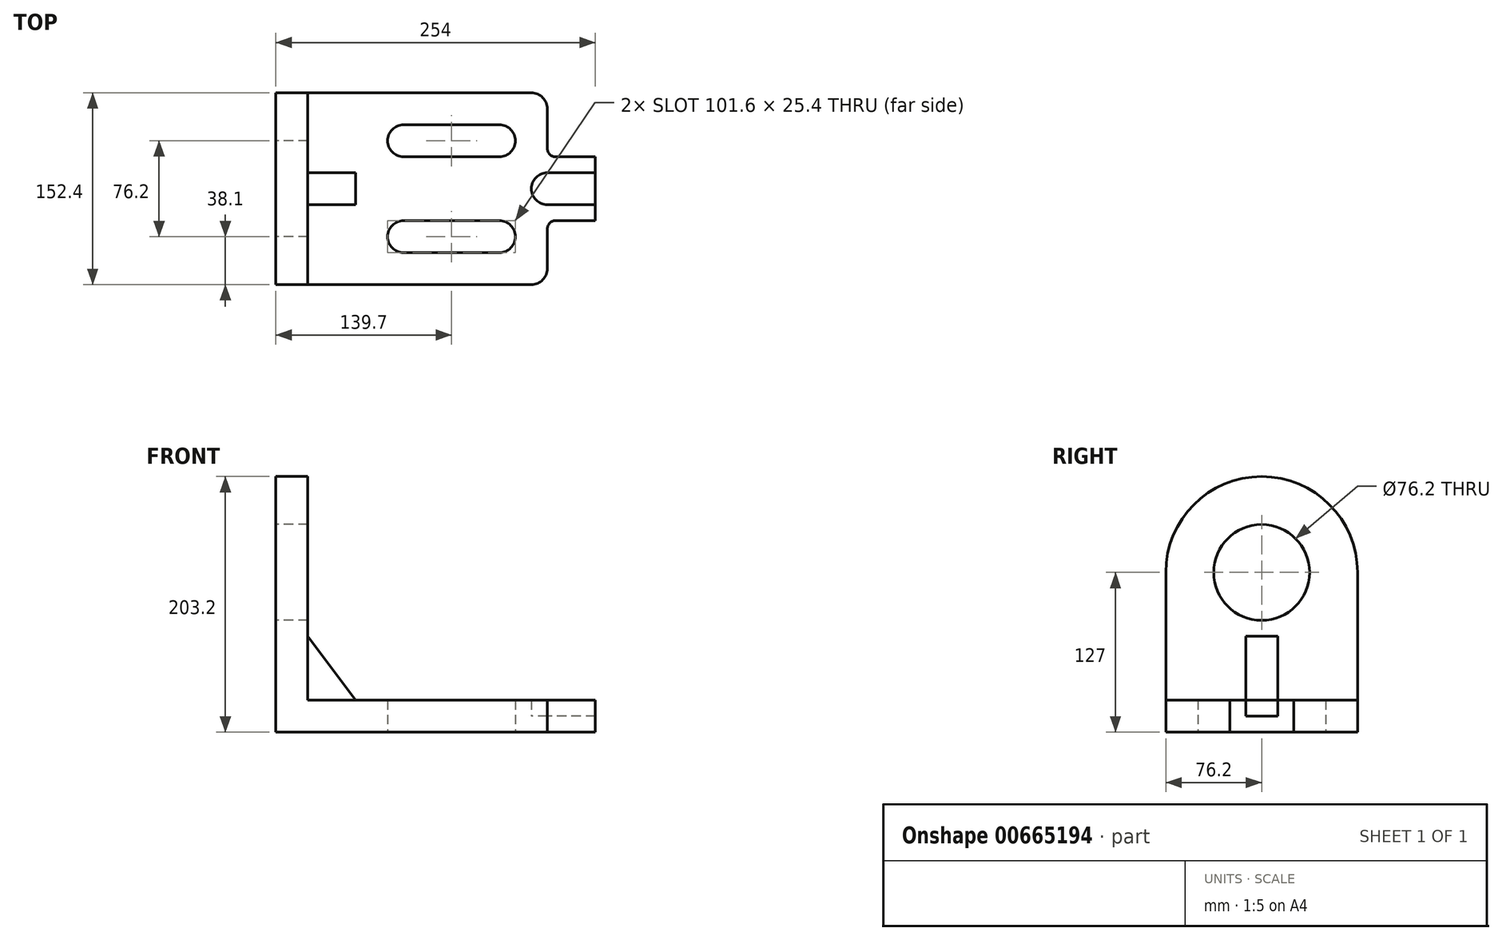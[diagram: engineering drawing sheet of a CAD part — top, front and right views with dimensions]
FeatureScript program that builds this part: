
annotation { "Feature Type Name" : "Feature", "Feature Type Description" : "" }
export const myFeature = defineFeature(function(context is Context, id is Id, definition is map)
    precondition{}
    {
        {
            var Q0;
            Q0=qCreatedBy(makeId("Top.planeOp"),FACE);
            var sketch = newSketch(context, id + "F0", { "sketchPlane" : qUnion([Q0])});
            skLineSegment(sketch, "E0", {"start": v(0, 0) * mm, "end": v(203.2, 0) * mm});
            skLineSegment(sketch, "E1", {"start": v(215.9, 12.7) * mm, "end": v(215.9, 44.45) * mm});
            skLineSegment(sketch, "E2", {"start": v(222.25, 50.8) * mm, "end": v(254, 50.8) * mm});
            skLineSegment(sketch, "E3", {"start": v(254, 50.8) * mm, "end": v(254, 63.5) * mm});
            skLineSegment(sketch, "E4", {"start": v(254, 63.5) * mm, "end": v(215.9, 63.5) * mm});
            skLineSegment(sketch, "E5", {"start": v(215.9, 88.9) * mm, "end": v(254, 88.9) * mm});
            skLineSegment(sketch, "E6", {"start": v(254, 88.9) * mm, "end": v(254, 101.6) * mm});
            skLineSegment(sketch, "E7", {"start": v(254, 101.6) * mm, "end": v(222.25, 101.6) * mm});
            skLineSegment(sketch, "E8", {"start": v(215.9, 107.95) * mm, "end": v(215.9, 139.7) * mm});
            skLineSegment(sketch, "E9", {"start": v(203.2, 152.4) * mm, "end": v(0, 152.4) * mm});
            skLineSegment(sketch, "E10", {"start": v(0, 152.4) * mm, "end": v(0, 0) * mm});
            skPoint(sketch, "E11.visualSharp", {"position": v(215.9, 152.4) * mm});
            skArc(sketch, "E11.filletArc", {"start": v(215.9, 139.7) * mm, "mid": v(212.18, 148.68) * mm, "end": v(203.2, 152.4) * mm});
            skPoint(sketch, "E12.visualSharp", {"position": v(215.9, 0) * mm});
            skArc(sketch, "E12.filletArc", {"start": v(203.2, 0) * mm, "mid": v(212.18, 3.72) * mm, "end": v(215.9, 12.7) * mm});
            skPoint(sketch, "E13.visualSharp", {"position": v(215.9, 50.8) * mm});
            skArc(sketch, "E13.filletArc", {"start": v(222.25, 50.8) * mm, "mid": v(217.76, 48.94) * mm, "end": v(215.9, 44.45) * mm});
            skPoint(sketch, "E14.visualSharp", {"position": v(215.9, 101.6) * mm});
            skArc(sketch, "E14.filletArc", {"start": v(215.9, 107.95) * mm, "mid": v(217.76, 103.46) * mm, "end": v(222.25, 101.6) * mm});
            skArc(sketch, "E15", {"start": v(215.9, 88.9) * mm, "mid": v(203.2, 76.2) * mm, "end": v(215.9, 63.5) * mm});
            skArc(sketch, "E16", {"start": v(101.6, 127) * mm, "mid": v(88.9, 114.3) * mm, "end": v(101.6, 101.6) * mm});
            skArc(sketch, "E17", {"start": v(177.8, 101.6) * mm, "mid": v(190.5, 114.3) * mm, "end": v(177.8, 127) * mm});
            skArc(sketch, "E18", {"start": v(101.6, 50.8) * mm, "mid": v(88.9, 38.1) * mm, "end": v(101.6, 25.4) * mm});
            skArc(sketch, "E19", {"start": v(177.8, 25.4) * mm, "mid": v(190.5, 38.1) * mm, "end": v(177.8, 50.8) * mm});
            skLineSegment(sketch, "E20", {"start": v(101.6, 127) * mm, "end": v(177.8, 127) * mm});
            skLineSegment(sketch, "E21", {"start": v(101.6, 101.6) * mm, "end": v(177.8, 101.6) * mm});
            skLineSegment(sketch, "E22", {"start": v(101.6, 25.4) * mm, "end": v(177.8, 25.4) * mm});
            skLineSegment(sketch, "E23", {"start": v(101.6, 50.8) * mm, "end": v(177.8, 50.8) * mm});
            skLineSegment(sketch, "E24", {"start": v(254, 88.9) * mm, "end": v(254, 63.5) * mm});
            skSolve(sketch);
        }
        {
            var Q0;
            Q0=makeQuery(id+"F0.imprint","IMPRINT",FACE,{"disambiguationData":[TD([[makeQuery(id+"F0.imprint","IMPRINT",EDGE,{"derivedFrom":sQuery(id+"F0.wireOp",EDGE,"E0")}),1.0]])]});
            extrude(context, id + "F1", {"entities" : qUnion([Q0]), "endBound" : BoundingType.SYMMETRIC, "depth" : 25.4 * mm, "offsetDistance" : 25.4 * mm});
        }
        {
            var Q0;
            Q0=makeQuery(id+"F0.imprint","IMPRINT",FACE,{"disambiguationData":[TD([[makeQuery(id+"F0.imprint","IMPRINT",EDGE,{"derivedFrom":sQuery(id+"F0.wireOp",EDGE,"E4")}),-1.0]])]});
            extrude(context, id + "F2", {"entities" : qUnion([Q0]), "operationType" : NewBodyOperationType.ADD, "oppositeDirection" : true, "depth" : 12.7 * mm, "offsetDistance" : 25.4 * mm});
        }
        {
            var Q0;
            Q0=makeQuery(id+"F1.opExtrude","SWEPT_FACE",FACE,{"disambiguationData":[OSD([sQuery(id+"F0.wireOp",EDGE,"E10")])]});
            var sketch = newSketch(context, id + "F3", { "sketchPlane" : qUnion([Q0])});
            skLineSegment(sketch, "E25", {"start": v(0, 12.7) * mm, "end": v(0, 114.3) * mm});
            skLineSegment(sketch, "E26", {"start": v(-152.4, 12.7) * mm, "end": v(-152.4, 114.3) * mm});
            skArc(sketch, "E27", {"start": v(0, 114.3) * mm, "mid": v(-76.2, 190.5) * mm, "end": v(-152.4, 114.3) * mm});
            skPoint(sketch, "E27.third.point", {"position": v(-76.2, 190.5) * mm});
            skCircle(sketch, "E28", {"center": v(-76.2, 114.3) * mm, "radius": 38.1 * mm});
            skSolve(sketch);
        }
        {
            var Q0;
            Q0=makeQuery(id+"F3.imprint","IMPRINT",FACE,{"disambiguationData":[TD([[makeQuery(id+"F3.imprint","IMPRINT",EDGE,{"derivedFrom":sQuery(id+"F3.wireOp",EDGE,"E25")}),1.0]])]});
            extrude(context, id + "F4", {"entities" : qUnion([Q0]), "operationType" : NewBodyOperationType.ADD, "oppositeDirection" : true, "depth" : 25.4 * mm, "offsetDistance" : 25.4 * mm});
        }
        {
            var Q0;
            Q0=makeQuery(id+"F4.boolean.opBoolean","MERGE",FACE,{"derivedFrom":[makeQuery(id+"F1.opExtrude","SWEPT_FACE",FACE,{"disambiguationData":[OSD([sQuery(id+"F0.wireOp",EDGE,"E0")])]}),makeQuery(id+"F4.opExtrude","SWEPT_FACE",FACE,{"disambiguationData":[OSD([sQuery(id+"F3.wireOp",EDGE,"E25")])]})]});
            cPlane(context, id + "F5", {"entities" : qUnion([Q0]), "cplaneType" : CPlaneType.OFFSET, "offset" : 76.2 * mm, "oppositeDirection" : true, "width" : 152.4 * mm, "height" : 152.4 * mm});
        }
        {
            var Q0;
            Q0=qCreatedBy(id+"F5.planeOp",FACE);
            var sketch = newSketch(context, id + "F6", { "sketchPlane" : qUnion([Q0])});
            skLineSegment(sketch, "E29", {"start": v(25.4, 63.5) * mm, "end": v(63.5, 12.7) * mm});
            skLineSegment(sketch, "E30", {"start": v(63.5, 12.7) * mm, "end": v(25.4, 12.7) * mm});
            skLineSegment(sketch, "E31", {"start": v(25.4, 12.7) * mm, "end": v(25.4, 63.5) * mm});
            skSolve(sketch);
        }
        {
            var Q0;
            Q0=makeQuery(id+"F6.imprint","IMPRINT",FACE,{"disambiguationData":[TD([[makeQuery(id+"F6.imprint","IMPRINT",EDGE,{"derivedFrom":sQuery(id+"F6.wireOp",EDGE,"E29")}),-1.0]])]});
            extrude(context, id + "F7", {"entities" : qUnion([Q0]), "operationType" : NewBodyOperationType.ADD, "endBound" : BoundingType.SYMMETRIC, "depth" : 25.4 * mm, "offsetDistance" : 25.4 * mm});
        }
    });
